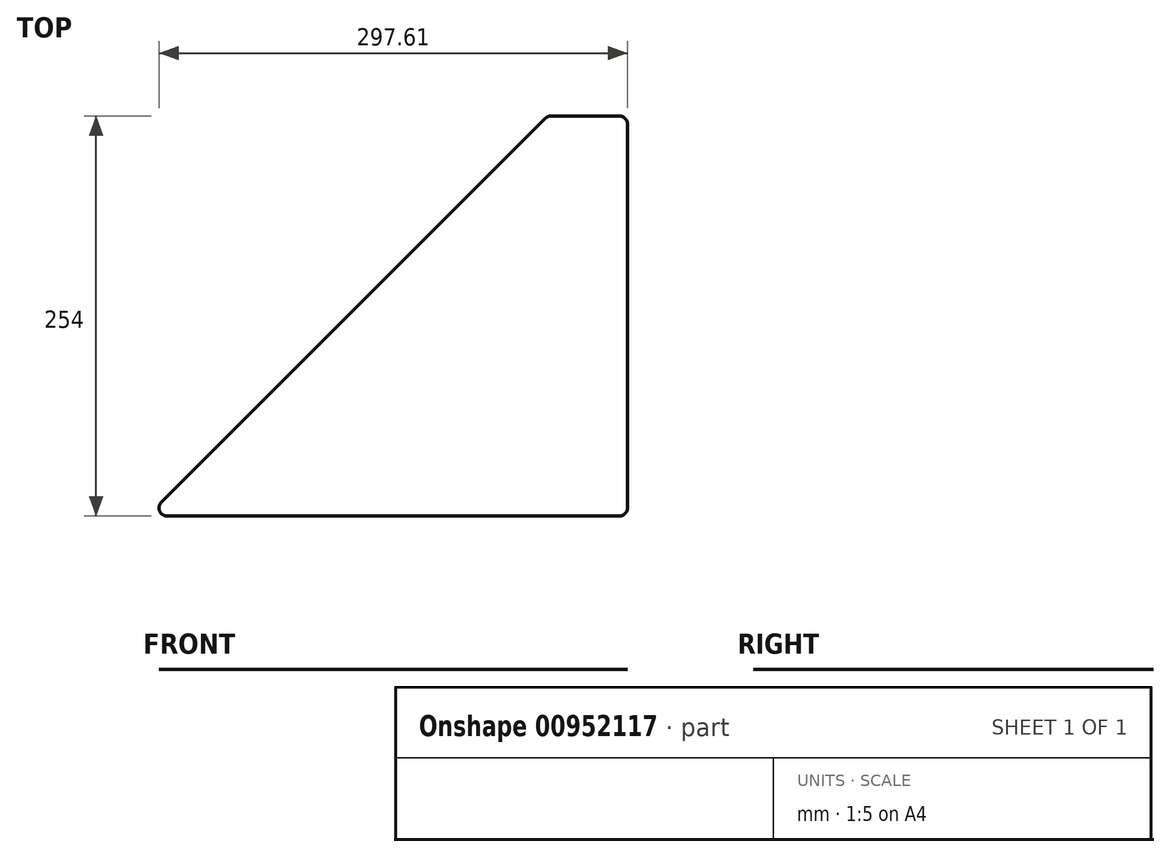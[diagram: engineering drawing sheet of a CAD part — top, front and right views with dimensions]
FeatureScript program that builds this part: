
annotation { "Feature Type Name" : "Feature", "Feature Type Description" : "" }
export const myFeature = defineFeature(function(context is Context, id is Id, definition is map)
    precondition{}
    {
        {
            var Q0;
            Q0=qCreatedBy(makeId("Top.planeOp"),FACE);
            var sketch = newSketch(context, id + "F0", { "sketchPlane" : qUnion([Q0])});
            skLineSegment(sketch, "E0", {"start": v(137.68, 231.95) * mm, "end": v(86.88, 231.95) * mm});
            skLineSegment(sketch, "E1", {"start": v(86.88, 231.95) * mm, "end": v(-167.12, -22.05) * mm});
            skLineSegment(sketch, "E2", {"start": v(-167.12, -22.05) * mm, "end": v(137.68, -22.05) * mm});
            skLineSegment(sketch, "E3", {"start": v(137.68, -22.05) * mm, "end": v(137.68, 231.95) * mm});
            skSolve(sketch);
        }
        {
            var Q0;
            Q0=makeQuery(id+"F0.imprint","IMPRINT",FACE,{"disambiguationData":[TD([[makeQuery(id+"F0.imprint","IMPRINT",EDGE,{"derivedFrom":sQuery(id+"F0.wireOp",EDGE,"E0")}),1.0]])]});
            extrude(context, id + "F1", {"entities" : qUnion([Q0]), "depth" : 1 / 203.2 * mm, "offsetDistance" : 25.4 * mm});
        }
        {
            var Q0;
            Q0=makeQuery(id+"F1.opExtrude","SWEPT_EDGE",EDGE,{"disambiguationData":[OSD([sQuery(id+"F0.wireOp",EDGE,"E0"),sQuery(id+"F0.wireOp",EDGE,"E1")])]});
            var Q1;
            Q1=makeQuery(id+"F1.opExtrude","SWEPT_EDGE",EDGE,{"disambiguationData":[OSD([sQuery(id+"F0.wireOp",EDGE,"E0"),sQuery(id+"F0.wireOp",EDGE,"E3")])]});
            var Q2;
            Q2=makeQuery(id+"F1.opExtrude","SWEPT_EDGE",EDGE,{"disambiguationData":[OSD([sQuery(id+"F0.wireOp",EDGE,"E2"),sQuery(id+"F0.wireOp",EDGE,"E3")])]});
            var Q3;
            Q3=makeQuery(id+"F1.opExtrude","SWEPT_EDGE",EDGE,{"disambiguationData":[OSD([sQuery(id+"F0.wireOp",EDGE,"E1"),sQuery(id+"F0.wireOp",EDGE,"E2")])]});
            fillet(context, id + "F2", {"entities" : qUnion([Q0, Q1, Q2, Q3]), "radius" : 5.08 * mm, "tangentPropagation" : true, "allowEdgeOverflow" : false});
        }
    });
